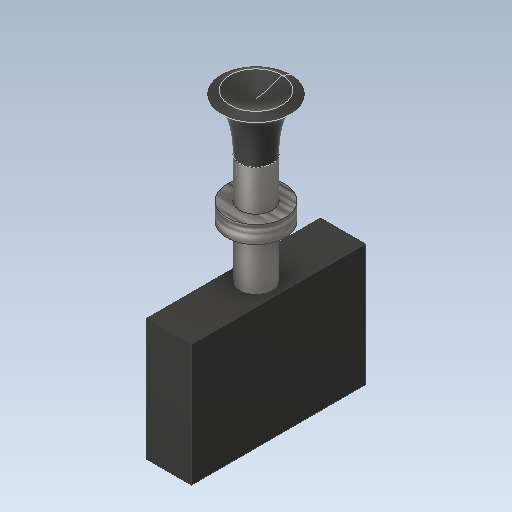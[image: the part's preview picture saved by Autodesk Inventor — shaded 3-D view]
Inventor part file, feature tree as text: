
AUTODESK INVENTOR PART (.ipt)
format: ipt  version: 2021 (Build 250183000, 183)  size: 225,792 bytes
history: native  units: mm
features: sketch x4, other x3, extrude x3, revolve x1, plane x1, imported_body x1
ambient origin geometry x8: Origin, YZ Plane, XZ Plane, XY Plane, X Axis, Y Axis, Z Axis, Center Point
bodies: Body1 (feature_tree), Body2 (feature_tree), Body3 (feature_tree), Body4 (feature_tree)
feature tree (13):
  other  "metal"
  extrude  "Extrusion1"  TaperAngle=0.0deg  [1 undecoded]
  revolve  "Revolution1"  Angle=90.0deg
  extrude  "Extrusion2"  Depth=21.0mm
  plane  "Work Plane1"
  extrude  "Extrusion3"  Depth=9.0mm
  sketch  "Sketch1"  dims[d0=19.0mm d1=0.0mm]
  sketch  "Sketch2"  dims[d2=6.0mm d3=90.0deg]
  other  "Top"
  sketch  "Sketch3"  dims[d4=30.0mm d5=21.0mm]
  imported_body  "Base"
  sketch  "Sketch4"  dims[d6=7.75mm d7=0.0mm d8=9.0mm d9=10.0mm d10=3.0mm d11=0.0mm]
  other  "Fastener"
note: 1 required parameter value undecoded (feature->parameter linkage not recoverable at this tier; creation-order binding heuristic only, values carry confidence <= 0.55)
